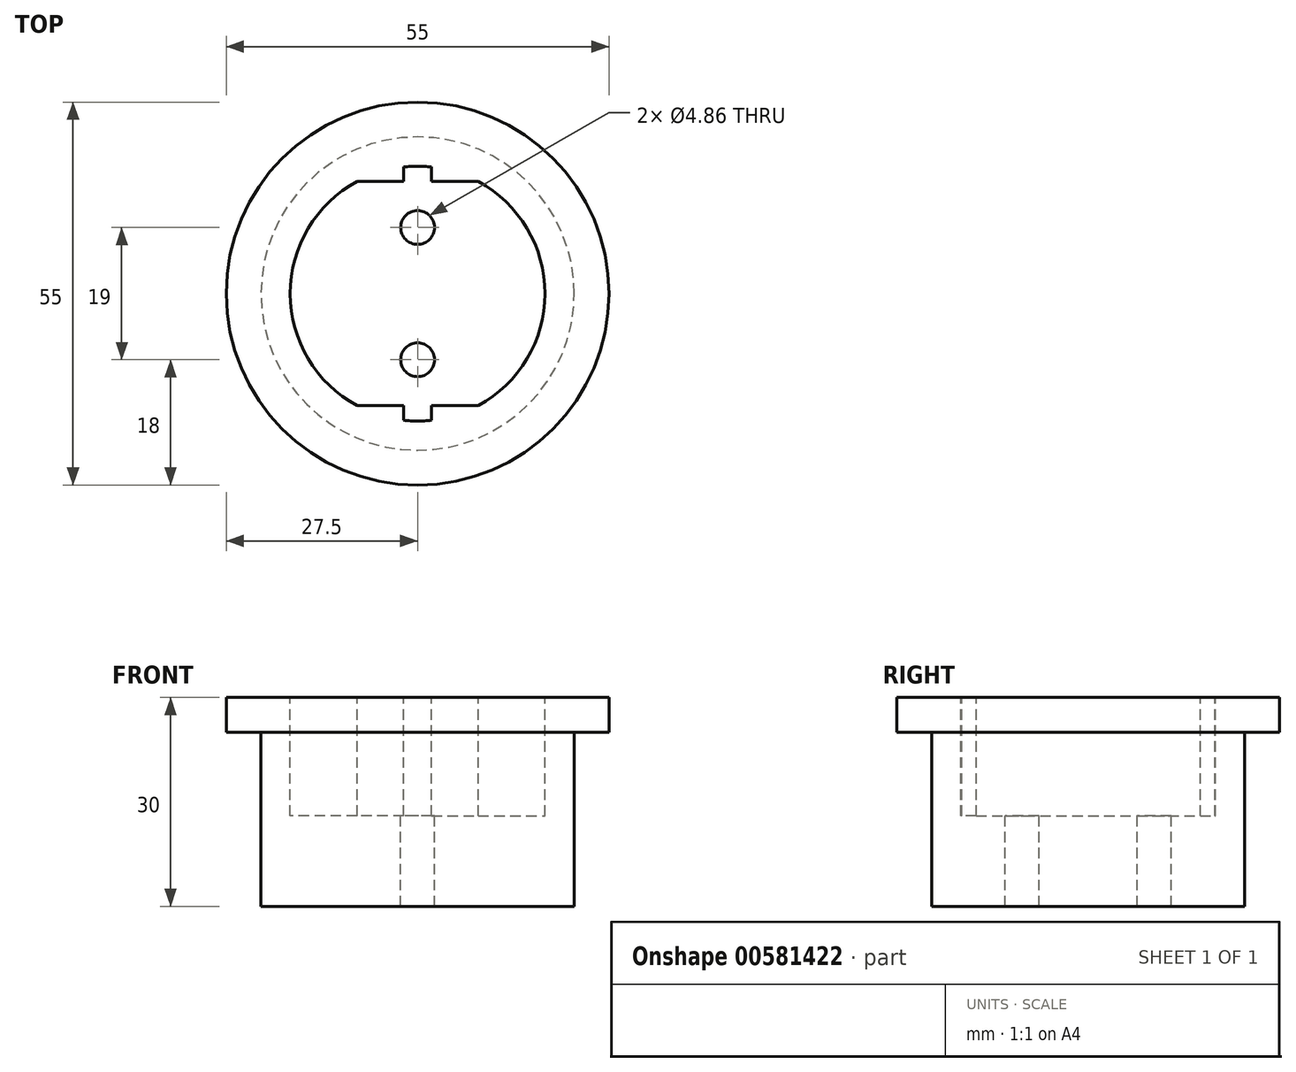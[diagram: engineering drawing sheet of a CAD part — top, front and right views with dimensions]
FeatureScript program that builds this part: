
annotation { "Feature Type Name" : "Feature", "Feature Type Description" : "" }
export const myFeature = defineFeature(function(context is Context, id is Id, definition is map)
    precondition{}
    {
        {
            var Q0;
            Q0=qCreatedBy(makeId("Front.planeOp"),FACE);
            var sketch = newSketch(context, id + "F0", { "sketchPlane" : qUnion([Q0])});
            skLineSegment(sketch, "E0", {"start": v(0, 0) * mm, "end": v(0, 30) * mm});
            skLineSegment(sketch, "E1", {"start": v(0, 30) * mm, "end": v(27.5, 30) * mm});
            skLineSegment(sketch, "E2", {"start": v(27.5, 30) * mm, "end": v(27.5, 25) * mm});
            skLineSegment(sketch, "E3", {"start": v(27.5, 25) * mm, "end": v(22.5, 25) * mm});
            skLineSegment(sketch, "E4", {"start": v(22.5, 25) * mm, "end": v(22.5, 0) * mm});
            skLineSegment(sketch, "E5", {"start": v(22.5, 0) * mm, "end": v(0, 0) * mm});
            skSolve(sketch);
        }
        {
            var Q0;
            Q0=makeQuery(id+"F0.imprint","IMPRINT",FACE,{"disambiguationData":[TD([[makeQuery(id+"F0.imprint","IMPRINT",EDGE,{"derivedFrom":sQuery(id+"F0.wireOp",EDGE,"E0")}),-1.0]])]});
            var Q1;
            Q1=sQuery(id+"F0.wireOp",EDGE,"E0");
            revolve(context, id + "F1", {"entities" : qUnion([Q0]), "axis" : qUnion([Q1]), "revolveType" : RevolveType.FULL});
        }
        {
            var Q0;
            Q0=makeQuery(id+"F1.opRevolve","SWEPT_FACE",FACE,{"disambiguationData":[OSD([sQuery(id+"F0.wireOp",EDGE,"E1")])]});
            var sketch = newSketch(context, id + "F2", { "sketchPlane" : qUnion([Q0])});
            skLineSegment(sketch, "E6", {"start": v(0, 0) * mm, "end": v(18.3, 0) * mm});
            skLineSegment(sketch, "E7", {"start": v(0, 0) * mm, "end": v(0, 16.1) * mm});
            skCircle(sketch, "E8", {"center": v(0, 0) * mm, "radius": 18.3 * mm});
            skLineSegment(sketch, "E9", {"start": v(0, 0) * mm, "end": v(0, -16.1) * mm});
            skLineSegment(sketch, "E10", {"start": v(8.7, 16.1) * mm, "end": v(-8.7, 16.1) * mm});
            skLineSegment(sketch, "E11", {"start": v(0, -16.1) * mm, "end": v(8.7, -16.1) * mm});
            skLineSegment(sketch, "E12", {"start": v(8.7, -16.1) * mm, "end": v(0, -16.1) * mm});
            skLineSegment(sketch, "E13", {"start": v(-8.7, -16.1) * mm, "end": v(0, -16.1) * mm});
            skLineSegment(sketch, "E14", {"start": v(0, 0) * mm, "end": v(0, 9.5) * mm});
            skLineSegment(sketch, "E15", {"start": v(0, 0) * mm, "end": v(0, -9.5) * mm});
            skLineSegment(sketch, "E16", {"start": v(-2, 16.1) * mm, "end": v(2, 16.1) * mm});
            skLineSegment(sketch, "E17", {"start": v(-2, -16.1) * mm, "end": v(2, -16.1) * mm});
            skLineSegment(sketch, "E18", {"start": v(-2, 16.1) * mm, "end": v(-2, 18.2) * mm});
            skLineSegment(sketch, "E19", {"start": v(2, 16.1) * mm, "end": v(2, 18.2) * mm});
            skLineSegment(sketch, "E20", {"start": v(-2, -16.1) * mm, "end": v(-2, -18.2) * mm});
            skLineSegment(sketch, "E21", {"start": v(2, -16.1) * mm, "end": v(2, -18.2) * mm});
            skLineSegment(sketch, "E22", {"start": v(0, 0) * mm, "end": v(10, 0) * mm});
            skSolve(sketch);
        }
        {
            var Q0;
            {var subQ0=sQuery(id+"F2.wireOp",EDGE,"E20");Q0=makeQuery(id+"F2.imprint","IMPRINT",FACE,{"disambiguationData":[TD([[makeQuery(id+"F2.imprint","IMPRINT",EDGE,{"derivedFrom":subQ0}),1.0]])]});}
            var Q1;
            {var subQ7=sQuery(id+"F2.wireOp",EDGE,"E7");Q1=makeQuery(id+"F2.imprint","IMPRINT",FACE,{"disambiguationData":[TD([[makeQuery(id+"F2.imprint","IMPRINT",EDGE,{"derivedFrom":subQ7}),1.0]])]});}
            var Q2;
            {var subQ0=sQuery(id+"F2.wireOp",EDGE,"E18");Q2=makeQuery(id+"F2.imprint","IMPRINT",FACE,{"disambiguationData":[TD([[makeQuery(id+"F2.imprint","IMPRINT",EDGE,{"derivedFrom":subQ0}),-1.0]])]});}
            var Q3;
            {var subQ6=sQuery(id+"F2.wireOp",EDGE,"E6");Q3=makeQuery(id+"F2.imprint","IMPRINT",FACE,{"disambiguationData":[TD([[makeQuery(id+"F2.imprint","IMPRINT",EDGE,{"derivedFrom":subQ6}),1.0]])]});}
            var Q4;
            {var subQ2=sQuery(id+"F2.wireOp",EDGE,"E6");Q4=makeQuery(id+"F2.imprint","IMPRINT",FACE,{"disambiguationData":[TD([[makeQuery(id+"F2.imprint","IMPRINT",EDGE,{"derivedFrom":subQ2}),-1.0]])]});}
            extrude(context, id + "F3", {"entities" : qUnion([Q0, Q1, Q2, Q3, Q4]), "operationType" : NewBodyOperationType.REMOVE, "oppositeDirection" : true, "depth" : 17 * mm, "offsetDistance" : 25 * mm});
        }
        {
            var Q0;
            Q0=sQuery(id+"F2.wireOp",VERTEX,"E14.end");
            var Q1;
            Q1=sQuery(id+"F2.wireOp",VERTEX,"E15.end");
            var Q2;
            Q2=makeQuery(id+"F1.opRevolve","SWEPT_BODY",BODY,{"disambiguationData":[OSD([sQuery(id+"F0.wireOp",EDGE,"E0"),sQuery(id+"F0.wireOp",EDGE,"E1"),sQuery(id+"F0.wireOp",EDGE,"E2"),sQuery(id+"F0.wireOp",EDGE,"E3"),sQuery(id+"F0.wireOp",EDGE,"E4"),sQuery(id+"F0.wireOp",EDGE,"E5")])]});
            hole(context, id + "F4", {"style" : HoleStyle.SIMPLE, "endStyle" : HoleEndStyle.THROUGH, "holeDiameter" : 4.86 * mm, "majorDiameter" : 5 * mm, "isTappedThrough" : true, "tappedDepth" : 12 * mm, "tapClearance" : 3, "locations" : qUnion([Q0, Q1]), "scope" : qUnion([Q2])});
        }
    });
